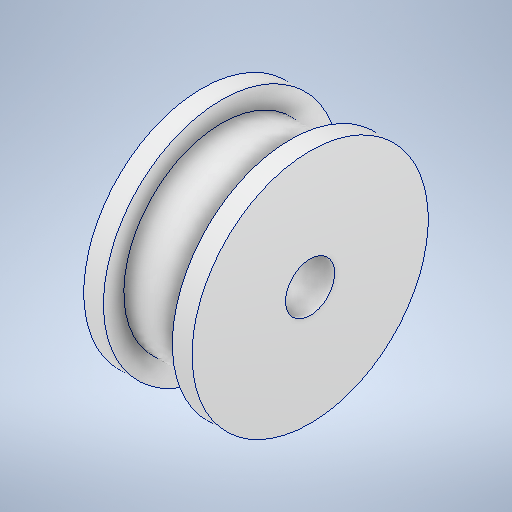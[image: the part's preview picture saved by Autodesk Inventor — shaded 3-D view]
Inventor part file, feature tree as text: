
AUTODESK INVENTOR PART (.ipt)
format: ipt  version: 2025.1 (Build 291241020, 241B)  size: 269,824 bytes
history: native  units: mm
features: revolve x1, mirror x1, sketch x1
ambient origin geometry x8: Origin, YZ Plane, XZ Plane, XY Plane, X Axis, Y Axis, Z Axis, Center Point
bodies: Solid1 (feature_tree)
feature tree (3):
  revolve  "Revolution1"  [1 undecoded]
  mirror  "Mirror2"
  sketch  "Sketch1"  dims[d0=5.5mm d1=3.5mm d2=9.93mm d3=12.0mm d4=2.5mm d5=360.0deg d8=1.0mm]
note: 1 required parameter value undecoded (feature->parameter linkage not recoverable at this tier; creation-order binding heuristic only, values carry confidence <= 0.55)
